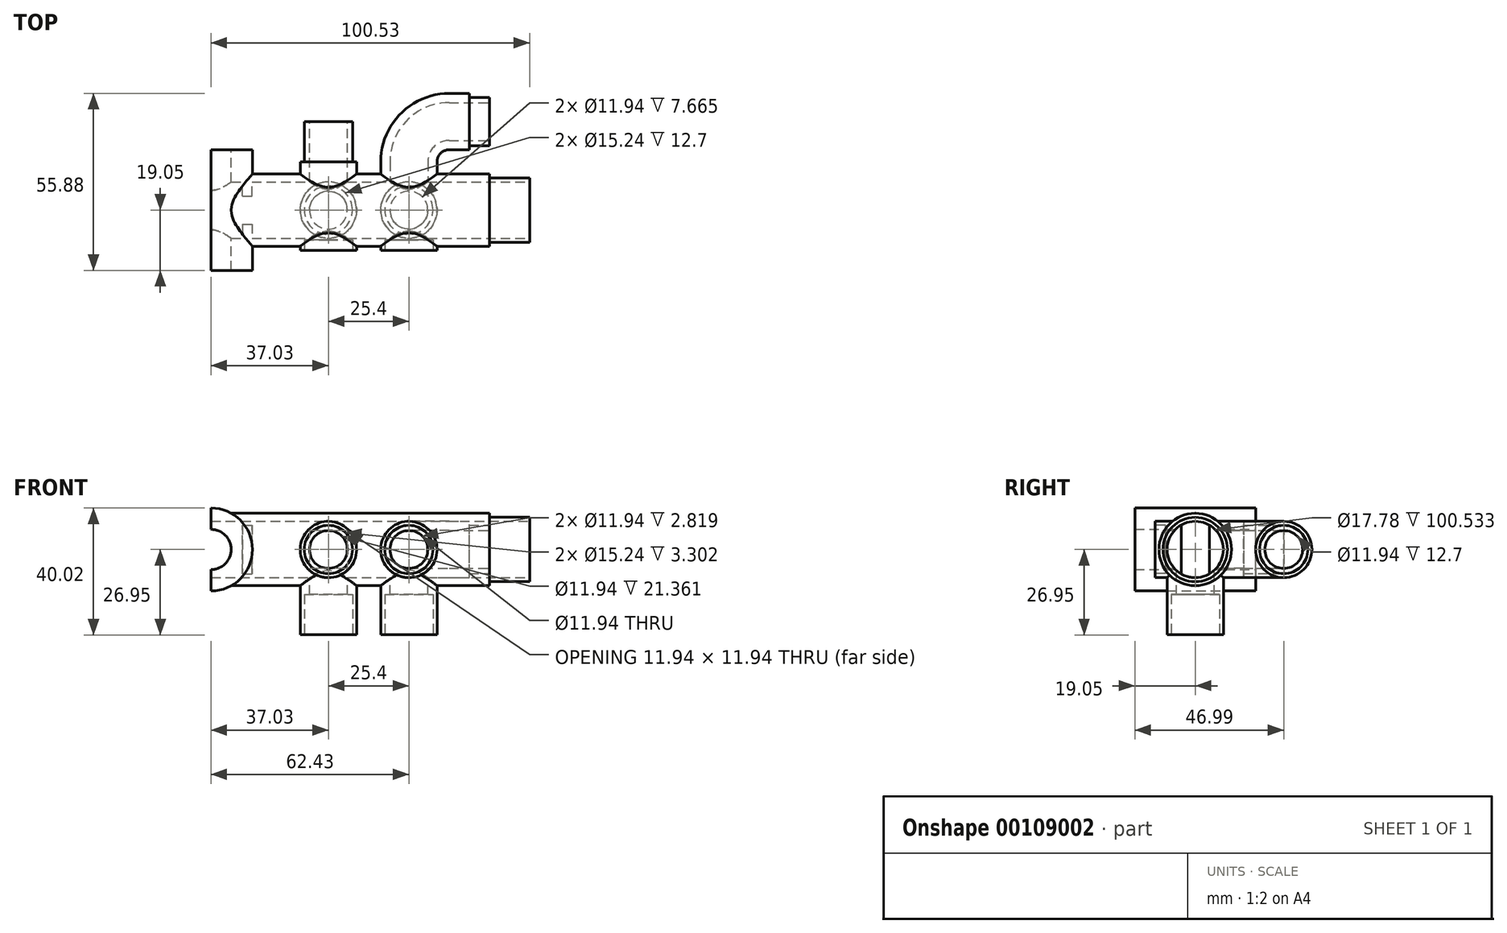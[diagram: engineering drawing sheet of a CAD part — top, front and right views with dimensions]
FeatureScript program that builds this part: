
annotation { "Feature Type Name" : "Feature", "Feature Type Description" : "" }
export const myFeature = defineFeature(function(context is Context, id is Id, definition is map)
    precondition{}
    {
        {
            var Q0;
            Q0=qCreatedBy(makeId("Front.planeOp"),FACE);
            var sketch = newSketch(context, id + "F0", { "sketchPlane" : qUnion([Q0])});
            skCircle(sketch, "E0", {"center": v(0, 0) * mm, "radius": 8.9 * mm});
            skCircle(sketch, "E1", {"center": v(0, 0) * mm, "radius": 5.97 * mm});
            skLineSegment(sketch, "E2", {"start": v(0, 0) * mm, "end": v(-25.4, 0) * mm});
            skCircle(sketch, "E3", {"center": v(-25.4, 0) * mm, "radius": 5.97 * mm});
            skCircle(sketch, "E4", {"center": v(-25.4, 0) * mm, "radius": 8.9 * mm});
            skLineSegment(sketch, "E5", {"start": v(-12.7, 0) * mm, "end": v(-12.7, 4.34) * mm});
            skLineSegment(sketch, "E6", {"start": v(-12.7, 4.34) * mm, "end": v(0, 4.34) * mm});
            skLineSegment(sketch, "E7", {"start": v(0, 0) * mm, "end": v(-38.1, 0) * mm});
            skLineSegment(sketch, "E8", {"start": v(-38.1, 0) * mm, "end": v(-49.53, 0) * mm});
            skSolve(sketch);
        }
        {
            var Q0;
            Q0=qCreatedBy(makeId("Right.planeOp"),FACE);
            var sketch = newSketch(context, id + "F1", { "sketchPlane" : qUnion([Q0])});
            skCircle(sketch, "E9", {"center": v(0, 0) * mm, "radius": 8.9 * mm});
            skCircle(sketch, "E10", {"center": v(0, 0) * mm, "radius": 11.43 * mm});
            skSolve(sketch);
        }
        {
            var Q0;
            Q0=qCreatedBy(makeId("Top.planeOp"),FACE);
            var sketch = newSketch(context, id + "F2", { "sketchPlane" : qUnion([Q0])});
            skCircle(sketch, "E11", {"center": v(0, 0) * mm, "radius": 5.97 * mm});
            skCircle(sketch, "E12", {"center": v(0, 0) * mm, "radius": 8.9 * mm});
            skLineSegment(sketch, "E13", {"start": v(0, 0) * mm, "end": v(-25.4, 0) * mm});
            skCircle(sketch, "E14", {"center": v(-25.4, 0) * mm, "radius": 5.97 * mm});
            skCircle(sketch, "E15", {"center": v(-25.4, 0) * mm, "radius": 8.9 * mm});
            skSolve(sketch);
        }
        {
            var Q0;
            Q0=makeQuery(id+"F1.imprint","IMPRINT",FACE,{"disambiguationData":[TD([[makeQuery(id+"F1.imprint","IMPRINT",EDGE,{"derivedFrom":sQuery(id+"F1.wireOp",EDGE,"E9")}),-1.0]])]});
            extrude(context, id + "F3", {"entities" : qUnion([Q0]), "oppositeDirection" : true, "depth" : 56.08 * mm, "hasSecondDirection" : true, "secondDirectionOppositeDirection" : false, "secondDirectionDepth" : 25.4 * mm});
        }
        {
            var Q0;
            Q0=makeQuery(id+"F0.imprint","IMPRINT",FACE,{"disambiguationData":[TD([[makeQuery(id+"F0.imprint","IMPRINT",EDGE,{"derivedFrom":sQuery(id+"F0.wireOp",EDGE,"E0")}),1.0]])]});
            extrude(context, id + "F4", {"entities" : qUnion([Q0]), "depth" : 12.7 * mm});
        }
        {
            var Q0;
            Q0=makeQuery(id+"F0.imprint","IMPRINT",FACE,{"disambiguationData":[TD([[makeQuery(id+"F0.imprint","IMPRINT",EDGE,{"derivedFrom":sQuery(id+"F0.wireOp",EDGE,"E3")}),-1.0]])]});
            extrude(context, id + "F5", {"entities" : qUnion([Q0]), "depth" : 12.7 * mm});
        }
        {
            var Q0;
            Q0=makeQuery(id+"F2.imprint","IMPRINT",FACE,{"disambiguationData":[TD([[makeQuery(id+"F2.imprint","IMPRINT",EDGE,{"derivedFrom":sQuery(id+"F2.wireOp",EDGE,"E14")}),-1.0]])]});
            extrude(context, id + "F6", {"entities" : qUnion([Q0]), "operationType" : NewBodyOperationType.ADD, "oppositeDirection" : true, "depth" : 26.95 * mm});
        }
        {
            var Q0;
            Q0=makeQuery(id+"F2.imprint","IMPRINT",FACE,{"disambiguationData":[TD([[makeQuery(id+"F2.imprint","IMPRINT",EDGE,{"derivedFrom":sQuery(id+"F2.wireOp",EDGE,"E11")}),-1.0]])]});
            extrude(context, id + "F7", {"entities" : qUnion([Q0]), "operationType" : NewBodyOperationType.ADD, "oppositeDirection" : true, "depth" : 26.95 * mm});
        }
        {
            var Q0;
            Q0=makeQuery(id+"F1.imprint","IMPRINT",FACE,{"disambiguationData":[TD([[makeQuery(id+"F1.imprint","IMPRINT",EDGE,{"derivedFrom":sQuery(id+"F1.wireOp",EDGE,"E9")}),1.0]])]});
            extrude(context, id + "F8", {"entities" : qUnion([Q0]), "operationType" : NewBodyOperationType.REMOVE, "depth" : 25.4 * mm, "hasSecondDirection" : true, "secondDirectionOppositeDirection" : true, "secondDirectionDepth" : 48.1 * mm});
        }
        {
            var Q0;
            Q0=makeQuery(id+"F2.imprint","IMPRINT",FACE,{"disambiguationData":[TD([[makeQuery(id+"F2.imprint","IMPRINT",EDGE,{"derivedFrom":sQuery(id+"F2.wireOp",EDGE,"E11")}),1.0]])]});
            extrude(context, id + "F9", {"entities" : qUnion([Q0]), "operationType" : NewBodyOperationType.REMOVE, "oppositeDirection" : true, "depth" : 25.4 * mm});
        }
        {
            var Q0;
            Q0=makeQuery(id+"F2.imprint","IMPRINT",FACE,{"disambiguationData":[TD([[makeQuery(id+"F2.imprint","IMPRINT",EDGE,{"derivedFrom":sQuery(id+"F2.wireOp",EDGE,"E14")}),1.0]])]});
            extrude(context, id + "F10", {"entities" : qUnion([Q0]), "operationType" : NewBodyOperationType.REMOVE, "oppositeDirection" : true, "depth" : 25.4 * mm});
        }
        {
            var Q0;
            Q0=makeQuery(id+"F0.imprint","IMPRINT",FACE,{"disambiguationData":[TD([[makeQuery(id+"F0.imprint","IMPRINT",EDGE,{"derivedFrom":sQuery(id+"F0.wireOp",EDGE,"E3")}),1.0]])]});
            extrude(context, id + "F11", {"entities" : qUnion([Q0]), "operationType" : NewBodyOperationType.REMOVE, "depth" : 25.4 * mm, "hasSecondDirection" : true, "secondDirectionOppositeDirection" : true, "secondDirectionDepth" : 25.4 * mm});
        }
        {
            var Q0;
            Q0=makeQuery(id+"F0.imprint","IMPRINT",FACE,{"disambiguationData":[TD([[makeQuery(id+"F0.imprint","IMPRINT",EDGE,{"derivedFrom":sQuery(id+"F0.wireOp",EDGE,"E1")}),1.0]])]});
            extrude(context, id + "F12", {"entities" : qUnion([Q0]), "operationType" : NewBodyOperationType.REMOVE, "oppositeDirection" : true, "depth" : 25.4 * mm, "hasSecondDirection" : true, "secondDirectionOppositeDirection" : false, "secondDirectionDepth" : 25.4 * mm});
        }
        {
            var Q0;
            Q0=makeQuery(id+"F5.opExtrude","CAP_FACE",FACE,{"disambiguationData":[OSD([sQuery(id+"F0.wireOp",EDGE,"E3"),sQuery(id+"F0.wireOp",EDGE,"E4")])],"isStart":false});
            var sketch = newSketch(context, id + "F13", { "sketchPlane" : qUnion([Q0])});
            skCircle(sketch, "E16", {"center": v(-25.4, 0) * mm, "radius": 7.62 * mm});
            skSolve(sketch);
        }
        {
            var Q0;
            Q0=makeQuery(id+"F4.opExtrude","CAP_FACE",FACE,{"disambiguationData":[OSD([sQuery(id+"F0.wireOp",EDGE,"E0"),sQuery(id+"F0.wireOp",EDGE,"E1")])],"isStart":false});
            var sketch = newSketch(context, id + "F14", { "sketchPlane" : qUnion([Q0])});
            skCircle(sketch, "E17", {"center": v(0, 0) * mm, "radius": 7.62 * mm});
            skSolve(sketch);
        }
        {
            var Q0;
            Q0=qCreatedBy(makeId("Top.planeOp"),FACE);
            var sketch = newSketch(context, id + "F15", { "sketchPlane" : qUnion([Q0])});
            skLineSegment(sketch, "E18", {"start": v(0, 0) * mm, "end": v(0, 15.24) * mm});
            skArc(sketch, "E19", {"start": v(0, 15.24) * mm, "mid": v(3.72, 24.22) * mm, "end": v(12.7, 27.94) * mm});
            skLineSegment(sketch, "E20", {"start": v(12.7, 27.94) * mm, "end": v(25.4, 27.94) * mm});
            skLineSegment(sketch, "E21", {"start": v(0, 0) * mm, "end": v(-25.4, 0) * mm});
            skLineSegment(sketch, "E22", {"start": v(-25.4, 0) * mm, "end": v(-25.4, 15.24) * mm});
            skLineSegment(sketch, "E23", {"start": v(-25.4, 15.24) * mm, "end": v(-25.4, 27.94) * mm});
            skSolve(sketch);
        }
        {
            var Q0;
            Q0=makeQuery(id+"F0.imprint","IMPRINT",FACE,{"disambiguationData":[TD([[makeQuery(id+"F0.imprint","IMPRINT",EDGE,{"derivedFrom":sQuery(id+"F0.wireOp",EDGE,"E3")}),-1.0]])]});
            var Q1;
            Q1=sQuery(id+"F15.wireOp",EDGE,"E22");
            var Q2;
            Q2=sQuery(id+"F15.wireOp",EDGE,"E23");
            sweep(context, id + "F16", {"operationType" : NewBodyOperationType.ADD, "profiles" : qUnion([Q0]), "path" : qUnion([Q1, Q2])});
        }
        {
            var Q0;
            Q0=makeQuery(id+"F0.imprint","IMPRINT",FACE,{"disambiguationData":[TD([[makeQuery(id+"F0.imprint","IMPRINT",EDGE,{"derivedFrom":sQuery(id+"F0.wireOp",EDGE,"E0")}),1.0]])]});
            var Q1;
            Q1=sQuery(id+"F15.wireOp",EDGE,"E18");
            var Q2;
            Q2=sQuery(id+"F15.wireOp",EDGE,"E19");
            var Q3;
            Q3=sQuery(id+"F15.wireOp",EDGE,"E20");
            sweep(context, id + "F17", {"operationType" : NewBodyOperationType.ADD, "profiles" : qUnion([Q0]), "path" : qUnion([Q1, Q2, Q3])});
        }
        {
            var Q0;
            Q0=makeQuery(id+"F1.imprint","IMPRINT",FACE,{"disambiguationData":[TD([[makeQuery(id+"F1.imprint","IMPRINT",EDGE,{"derivedFrom":sQuery(id+"F1.wireOp",EDGE,"E9")}),1.0]])]});
            extrude(context, id + "F18", {"entities" : qUnion([Q0]), "operationType" : NewBodyOperationType.REMOVE, "depth" : 25.4 * mm, "hasSecondDirection" : true, "secondDirectionOppositeDirection" : true, "secondDirectionDepth" : 37.53 * mm});
        }
        {
            var Q0;
            Q0=makeQuery(id+"F17.opSweep","CAP_FACE",FACE,{"disambiguationData":[OSD([sQuery(id+"F0.wireOp",EDGE,"E0"),sQuery(id+"F0.wireOp",EDGE,"E1"),sQuery(id+"F15.wireOp",VERTEX,"E20.end")])],"isStart":false});
            var sketch = newSketch(context, id + "F19", { "sketchPlane" : qUnion([Q0])});
            skCircle(sketch, "E24", {"center": v(27.94, 0) * mm, "radius": 7.62 * mm});
            skSolve(sketch);
        }
        {
            var Q0;
            Q0=makeQuery(id+"F16.opSweep","CAP_FACE",FACE,{"disambiguationData":[OSD([sQuery(id+"F0.wireOp",EDGE,"E3"),sQuery(id+"F0.wireOp",EDGE,"E4"),sQuery(id+"F15.wireOp",VERTEX,"R4gBbVMg-ZXYU-ST5p-1KpP-Dd21gCYw7uKT.end")])],"isStart":false});
            var sketch = newSketch(context, id + "F20", { "sketchPlane" : qUnion([Q0])});
            skCircle(sketch, "E25", {"center": v(25.4, 0) * mm, "radius": 7.62 * mm});
            skSolve(sketch);
        }
        {
            var Q0;
            Q0=makeQuery(id+"F19.imprint","IMPRINT",FACE,{"disambiguationData":[TD([[makeQuery(id+"F19.imprint","IMPRINT",EDGE,{"derivedFrom":sQuery(id+"F19.wireOp",EDGE,"E24")}),-1.0]])]});
            extrude(context, id + "F21", {"entities" : qUnion([Q0]), "operationType" : NewBodyOperationType.REMOVE, "oppositeDirection" : true, "depth" : 6.35 * mm});
        }
        {
            var Q0;
            Q0=makeQuery(id+"F20.imprint","IMPRINT",FACE,{"disambiguationData":[TD([[makeQuery(id+"F20.imprint","IMPRINT",EDGE,{"derivedFrom":sQuery(id+"F20.wireOp",EDGE,"E25")}),-1.0]])]});
            extrude(context, id + "F22", {"entities" : qUnion([Q0]), "operationType" : NewBodyOperationType.REMOVE, "oppositeDirection" : true, "depth" : 12.7 * mm});
        }
        {
            var Q0;
            Q0=makeQuery(id+"F13.imprint","IMPRINT",FACE,{"disambiguationData":[TD([[makeQuery(id+"F13.imprint","IMPRINT",EDGE,{"derivedFrom":sQuery(id+"F13.wireOp",EDGE,"E16")}),1.0]])]});
            var Q1;
            Q1=makeQuery(id+"F14.imprint","IMPRINT",FACE,{"disambiguationData":[TD([[makeQuery(id+"F14.imprint","IMPRINT",EDGE,{"derivedFrom":sQuery(id+"F14.wireOp",EDGE,"E17")}),1.0]])]});
            extrude(context, id + "F23", {"entities" : qUnion([Q0, Q1]), "operationType" : NewBodyOperationType.REMOVE, "oppositeDirection" : true, "depth" : 3.3 * mm});
        }
        {
            var Q0;
            Q0=makeQuery(id+"F2.imprint","IMPRINT",FACE,{"disambiguationData":[TD([[makeQuery(id+"F2.imprint","IMPRINT",EDGE,{"derivedFrom":sQuery(id+"F2.wireOp",EDGE,"E14")}),1.0]])]});
            extrude(context, id + "F24", {"entities" : qUnion([Q0]), "operationType" : NewBodyOperationType.REMOVE, "oppositeDirection" : true, "depth" : 25.4 * mm});
        }
        {
            var Q0;
            Q0=makeQuery(id+"F2.imprint","IMPRINT",FACE,{"disambiguationData":[TD([[makeQuery(id+"F2.imprint","IMPRINT",EDGE,{"derivedFrom":sQuery(id+"F2.wireOp",EDGE,"E11")}),1.0]])]});
            extrude(context, id + "F25", {"entities" : qUnion([Q0]), "operationType" : NewBodyOperationType.REMOVE, "oppositeDirection" : true, "depth" : 25.4 * mm});
        }
        {
            var Q0;
            Q0=makeQuery(id+"F7.opExtrude","CAP_FACE",FACE,{"disambiguationData":[OSD([sQuery(id+"F2.wireOp",EDGE,"E11"),sQuery(id+"F2.wireOp",EDGE,"E12")])],"isStart":false});
            var sketch = newSketch(context, id + "F26", { "sketchPlane" : qUnion([Q0])});
            skCircle(sketch, "E26", {"center": v(0, 0) * mm, "radius": 7.62 * mm});
            skSolve(sketch);
        }
        {
            var Q0;
            Q0=makeQuery(id+"F6.opExtrude","CAP_FACE",FACE,{"disambiguationData":[OSD([sQuery(id+"F2.wireOp",EDGE,"E14"),sQuery(id+"F2.wireOp",EDGE,"E15")])],"isStart":false});
            var sketch = newSketch(context, id + "F27", { "sketchPlane" : qUnion([Q0])});
            skCircle(sketch, "E27", {"center": v(-25.4, 0) * mm, "radius": 7.62 * mm});
            skSolve(sketch);
        }
        {
            var Q0;
            Q0=makeQuery(id+"F27.imprint","IMPRINT",FACE,{"disambiguationData":[TD([[makeQuery(id+"F27.imprint","IMPRINT",EDGE,{"derivedFrom":sQuery(id+"F27.wireOp",EDGE,"E27")}),1.0]])]});
            var Q1;
            Q1=makeQuery(id+"F26.imprint","IMPRINT",FACE,{"disambiguationData":[TD([[makeQuery(id+"F26.imprint","IMPRINT",EDGE,{"derivedFrom":sQuery(id+"F26.wireOp",EDGE,"E26")}),1.0]])]});
            extrude(context, id + "F28", {"entities" : qUnion([Q0, Q1]), "operationType" : NewBodyOperationType.REMOVE, "oppositeDirection" : true, "depth" : 12.7 * mm});
        }
        {
            var Q0;
            Q0=makeQuery(id+"F3.opExtrude","CAP_FACE",FACE,{"disambiguationData":[OSD([sQuery(id+"F1.wireOp",EDGE,"E9"),sQuery(id+"F1.wireOp",EDGE,"E10")])],"isStart":true});
            var sketch = newSketch(context, id + "F29", { "sketchPlane" : qUnion([Q0])});
            skCircle(sketch, "E28", {"center": v(0, 0) * mm, "radius": 10.16 * mm});
            skSolve(sketch);
        }
        {
            var Q0;
            Q0=makeQuery(id+"F29.imprint","IMPRINT",FACE,{"disambiguationData":[TD([[makeQuery(id+"F29.imprint","IMPRINT",EDGE,{"derivedFrom":sQuery(id+"F29.wireOp",EDGE,"E28")}),1.0]])]});
            extrude(context, id + "F30", {"entities" : qUnion([Q0]), "operationType" : NewBodyOperationType.ADD, "depth" : 12.7 * mm});
        }
        {
            var Q0;
            Q0=qCreatedBy(makeId("Top.planeOp"),FACE);
            var sketch = newSketch(context, id + "F31", { "sketchPlane" : qUnion([Q0])});
            skCircle(sketch, "E29", {"center": v(-62.43, 0) * mm, "radius": 6.35 * mm});
            skCircle(sketch, "E30", {"center": v(-62.43, 0) * mm, "radius": 8.9 * mm});
            skLineSegment(sketch, "E31", {"start": v(-62.43, 0) * mm, "end": v(-56.08, 0) * mm});
            skLineSegment(sketch, "E32", {"start": v(-62.43, 0) * mm, "end": v(-62.43, 8.9) * mm});
            skLineSegment(sketch, "E33", {"start": v(-62.43, 0) * mm, "end": v(-62.43, -8.9) * mm});
            skSolve(sketch);
        }
        {
            var Q0;
            Q0=qCreatedBy(makeId("Front.planeOp"),FACE);
            var sketch = newSketch(context, id + "F32", { "sketchPlane" : qUnion([Q0])});
            skLineSegment(sketch, "E34", {"start": v(-56.08, 0) * mm, "end": v(-62.43, 0) * mm});
            skCircle(sketch, "E35", {"center": v(-62.43, 0) * mm, "radius": 6.35 * mm});
            skCircle(sketch, "E36", {"center": v(-62.43, 0) * mm, "radius": 13.07 * mm});
            skLineSegment(sketch, "E37", {"start": v(-62.43, 0) * mm, "end": v(-62.43, 13.07) * mm});
            skLineSegment(sketch, "E38", {"start": v(-62.43, 0) * mm, "end": v(-62.43, -13.07) * mm});
            skSolve(sketch);
        }
        {
            var Q0;
            {var subQ3=sQuery(id+"F32.wireOp",EDGE,"E35");var subQ5=makeQuery(id+"F32.imprint","INTERSECT",VERTEX,{"derivedFrom":[sQuery(id+"F32.wireOp",EDGE,"E34"),subQ3]});Q0=makeQuery(id+"F32.imprint","IMPRINT",FACE,{"disambiguationData":[TD([[makeQuery(id+"F32.imprint","IMPRINT",EDGE,{"disambiguationData":[TD([[subQ5,-1.0]])],"derivedFrom":subQ3}),-1.0]])]});}
            extrude(context, id + "F33", {"entities" : qUnion([Q0]), "operationType" : NewBodyOperationType.ADD, "depth" : 19.05 * mm, "hasSecondDirection" : true, "secondDirectionOppositeDirection" : true, "secondDirectionDepth" : 19.05 * mm});
        }
        {
            var Q0;
            Q0=makeQuery(id+"F1.imprint","IMPRINT",FACE,{"disambiguationData":[TD([[makeQuery(id+"F1.imprint","IMPRINT",EDGE,{"derivedFrom":sQuery(id+"F1.wireOp",EDGE,"E9")}),1.0]])]});
            extrude(context, id + "F34", {"entities" : qUnion([Q0]), "operationType" : NewBodyOperationType.REMOVE, "oppositeDirection" : true, "depth" : 76.92 * mm});
        }
        {
            var Q0;
            Q0=sQuery(id+"F0.wireOp",EDGE,"E8");
            var Q1;
            Q1=sQuery(id+"F0.wireOp",VERTEX,"E8.end");
            cPlane(context, id + "F35", {"entities" : qUnion([Q0, Q1]), "cplaneType" : CPlaneType.LINE_POINT, "offset" : 25.4 * mm, "width" : 152.4 * mm, "height" : 152.4 * mm});
        }
        {
            var Q0;
            Q0=qCreatedBy(id+"F35.planeOp",FACE);
            var sketch = newSketch(context, id + "F36", { "sketchPlane" : qUnion([Q0])});
            skCircle(sketch, "E39", {"center": v(0, 0) * mm, "radius": 4.45 * mm});
            skCircle(sketch, "E40", {"center": v(0, 0) * mm, "radius": 10.16 * mm});
            skLineSegment(sketch, "E41", {"start": v(-4.45, 0) * mm, "end": v(-4.45, 9.14) * mm});
            skLineSegment(sketch, "E42", {"start": v(-4.45, 0) * mm, "end": v(-4.44, -9.14) * mm});
            skLineSegment(sketch, "E43", {"start": v(4.45, 0) * mm, "end": v(4.45, 9.14) * mm});
            skLineSegment(sketch, "E44", {"start": v(4.45, 0) * mm, "end": v(4.44, -9.14) * mm});
            skSolve(sketch);
        }
        {
            var Q0;
            {var subQ0=sQuery(id+"F36.wireOp",EDGE,"E41");Q0=makeQuery(id+"F36.imprint","IMPRINT",FACE,{"disambiguationData":[TD([[makeQuery(id+"F36.imprint","IMPRINT",EDGE,{"derivedFrom":subQ0}),1.0]])]});}
            var Q1;
            {var subQ0=sQuery(id+"F36.wireOp",EDGE,"E43");Q1=makeQuery(id+"F36.imprint","IMPRINT",FACE,{"disambiguationData":[TD([[makeQuery(id+"F36.imprint","IMPRINT",EDGE,{"derivedFrom":subQ0}),-1.0]])]});}
            extrude(context, id + "F37", {"entities" : qUnion([Q0, Q1]), "operationType" : NewBodyOperationType.ADD, "depth" : 2.97 * mm});
        }
    });
